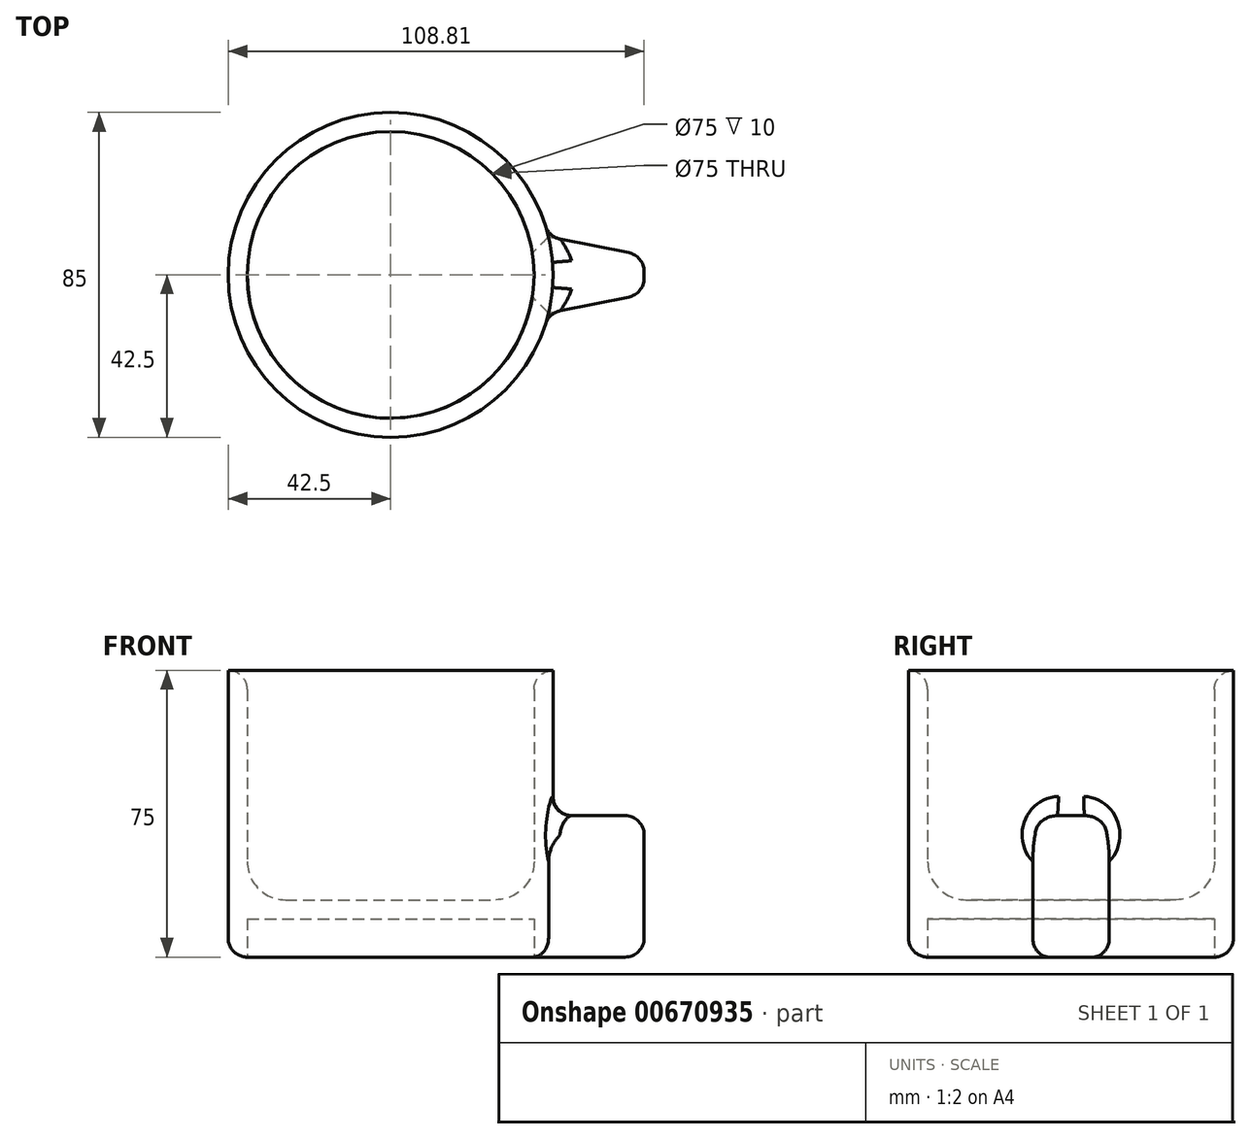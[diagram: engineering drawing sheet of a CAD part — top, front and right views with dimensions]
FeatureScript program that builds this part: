
annotation { "Feature Type Name" : "Feature", "Feature Type Description" : "" }
export const myFeature = defineFeature(function(context is Context, id is Id, definition is map)
    precondition{}
    {
        {
            var Q0;
            Q0=qCreatedBy(makeId("Front.planeOp"),FACE);
            var sketch = newSketch(context, id + "F0", { "sketchPlane" : qUnion([Q0])});
            skLineSegment(sketch, "E0", {"start": v(0, -27) * mm, "end": v(0, -22) * mm});
            skLineSegment(sketch, "E1", {"start": v(0, -22) * mm, "end": v(37.5, -22) * mm});
            skLineSegment(sketch, "E2", {"start": v(37.5, -22) * mm, "end": v(37.5, 38) * mm});
            skLineSegment(sketch, "E3", {"start": v(37.5, 38) * mm, "end": v(42.5, 38) * mm});
            skLineSegment(sketch, "E4", {"start": v(42.5, 38) * mm, "end": v(42.5, -37) * mm});
            skLineSegment(sketch, "E5", {"start": v(42.5, -37) * mm, "end": v(37.5, -37) * mm});
            skLineSegment(sketch, "E6", {"start": v(37.5, -37) * mm, "end": v(37.5, -27) * mm});
            skLineSegment(sketch, "E7", {"start": v(37.5, -27) * mm, "end": v(0, -27) * mm});
            skSolve(sketch);
        }
        {
            var Q0;
            Q0=qSketchRegion(id+"F0",true);
            var Q1;
            Q1=sQuery(id+"F0.wireOp",EDGE,"E0");
            revolve(context, id + "F1", {"entities" : qUnion([Q0]), "axis" : qUnion([Q1]), "revolveType" : RevolveType.FULL});
        }
        {
            var Q0;
            Q0=qCreatedBy(makeId("Top.planeOp"),FACE);
            var sketch = newSketch(context, id + "F2", { "sketchPlane" : qUnion([Q0])});
            skLineSegment(sketch, "E8", {"start": v(41.3, -10) * mm, "end": v(66.3, -5) * mm});
            skLineSegment(sketch, "E9", {"start": v(66.3, -5) * mm, "end": v(66.3, 5) * mm});
            skLineSegment(sketch, "E10", {"start": v(66.3, 5) * mm, "end": v(41.3, 10) * mm});
            skLineSegment(sketch, "E11", {"start": v(41.3, 10) * mm, "end": v(41.3, -10) * mm});
            skSolve(sketch);
        }
        {
            var Q0;
            Q0=qSketchRegion(id+"F2",true);
            extrude(context, id + "F3", {"entities" : qUnion([Q0]), "operationType" : NewBodyOperationType.ADD, "oppositeDirection" : true, "depth" : 37 * mm, "offsetDistance" : 25 * mm});
        }
        {
            var Q0;
            Q0=makeQuery(id+"F3.opExtrude","CAP_EDGE",EDGE,{"disambiguationData":[OSD([sQuery(id+"F2.wireOp",EDGE,"E8")])],"isStart":false});
            var Q1;
            Q1=makeQuery(id+"F1.opRevolve","SWEPT_EDGE",EDGE,{"disambiguationData":[OSD([sQuery(id+"F0.wireOp",EDGE,"E4"),sQuery(id+"F0.wireOp",EDGE,"E5")])]});
            var Q2;
            Q2=makeQuery(id+"F3.opExtrude","CAP_EDGE",EDGE,{"disambiguationData":[OSD([sQuery(id+"F2.wireOp",EDGE,"E10")])],"isStart":false});
            var Q3;
            Q3=makeQuery(id+"F3.opExtrude","CAP_EDGE",EDGE,{"disambiguationData":[OSD([sQuery(id+"F2.wireOp",EDGE,"E9")])],"isStart":false});
            var Q4;
            Q4=makeQuery(id+"F3.opExtrude","SWEPT_EDGE",EDGE,{"disambiguationData":[OSD([sQuery(id+"F2.wireOp",EDGE,"E8"),sQuery(id+"F2.wireOp",EDGE,"E9")])]});
            var Q5;
            Q5=makeQuery(id+"F3.opExtrude","SWEPT_EDGE",EDGE,{"disambiguationData":[OSD([sQuery(id+"F2.wireOp",EDGE,"E9"),sQuery(id+"F2.wireOp",EDGE,"E10")])]});
            var Q6;
            Q6=makeQuery(id+"F3.opExtrude","CAP_FACE",FACE,{"disambiguationData":[OSD([sQuery(id+"F2.wireOp",EDGE,"E8"),sQuery(id+"F2.wireOp",EDGE,"E9"),sQuery(id+"F2.wireOp",EDGE,"E10"),sQuery(id+"F2.wireOp",EDGE,"E11")])],"isStart":true});
            var Q7;
            Q7=makeQuery(id+"F1.opRevolve","SWEPT_EDGE",EDGE,{"disambiguationData":[OSD([sQuery(id+"F0.wireOp",EDGE,"E2"),sQuery(id+"F0.wireOp",EDGE,"E3")])]});
            fillet(context, id + "F4", {"entities" : qUnion([Q0, Q1, Q2, Q3, Q4, Q5, Q6, Q7]), "radius" : 5 * mm, "tangentPropagation" : true, "allowEdgeOverflow" : false});
        }
        {
            var Q0;
            Q0=makeQuery(id+"F1.opRevolve","SWEPT_FACE",FACE,{"disambiguationData":[OSD([sQuery(id+"F0.wireOp",EDGE,"E1")])]});
            fillet(context, id + "F5", {"entities" : qUnion([Q0]), "radius" : 10 * mm, "tangentPropagation" : true, "allowEdgeOverflow" : false});
        }
    });
